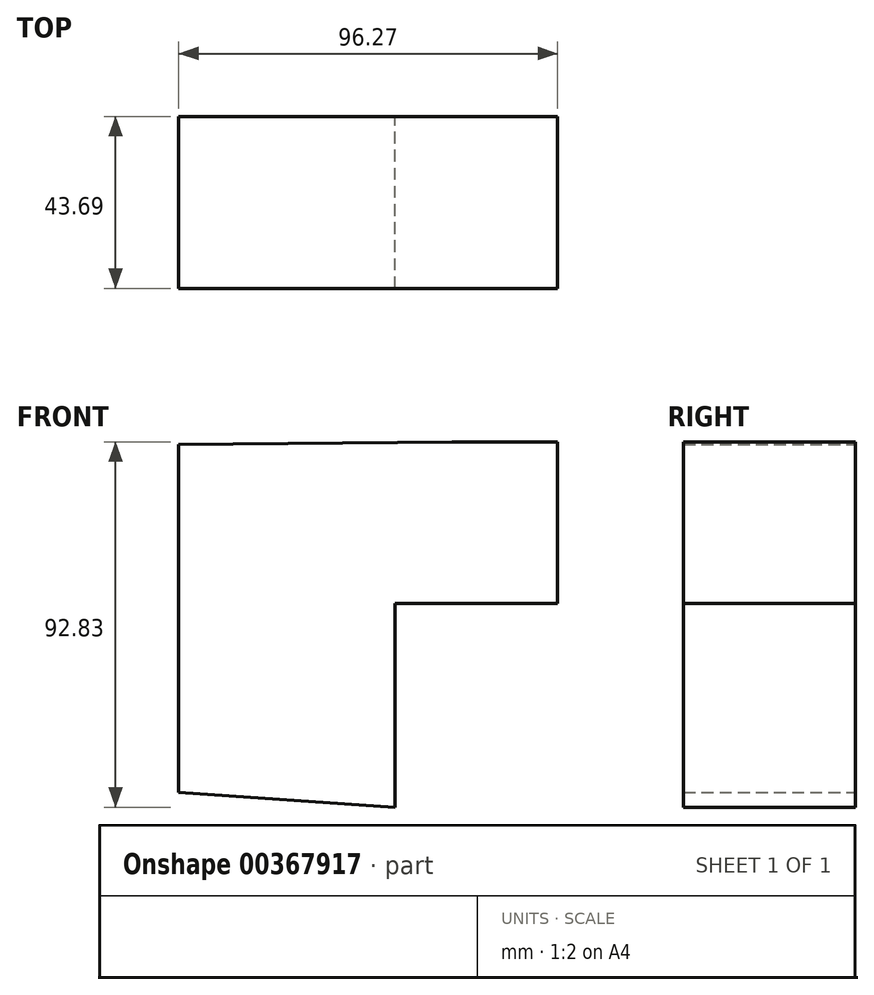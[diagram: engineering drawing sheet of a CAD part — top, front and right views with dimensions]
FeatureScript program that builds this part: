
annotation { "Feature Type Name" : "Feature", "Feature Type Description" : "" }
export const myFeature = defineFeature(function(context is Context, id is Id, definition is map)
    precondition{}
    {
        {
            var Q0;
            Q0=qCreatedBy(makeId("Front.planeOp"),FACE);
            var sketch = newSketch(context, id + "F0", { "sketchPlane" : qUnion([Q0])});
            skLineSegment(sketch, "E0", {"start": v(14.38, 41.1) * mm, "end": v(41.26, 41.1) * mm});
            skLineSegment(sketch, "E1", {"start": v(41.26, 41.1) * mm, "end": v(41.26, 0) * mm});
            skLineSegment(sketch, "E2", {"start": v(41.26, 0) * mm, "end": v(0, 0) * mm});
            skLineSegment(sketch, "E3", {"start": v(0, 0) * mm, "end": v(0, -51.73) * mm});
            skLineSegment(sketch, "E4", {"start": v(0, -51.73) * mm, "end": v(-55.01, -47.98) * mm});
            skLineSegment(sketch, "E5", {"start": v(-55.01, -47.98) * mm, "end": v(-55.01, 40.48) * mm});
            skLineSegment(sketch, "E6", {"start": v(-55.01, 40.48) * mm, "end": v(14.38, 41.1) * mm});
            skSolve(sketch);
        }
        {
            var Q0;
            Q0 = qSketchRegion(id + "F0", true);
            extrude(context, id + "F1", {"entities" : qUnion([Q0]), "depth" : 25.4 * mm});
        }
        {
            var Q0;
            Q0=makeQuery(id+"F1.opExtrude","CAP_FACE",FACE,{"disambiguationData":[OSD([sQuery(id+"F0.wireOp",EDGE,"E0"),sQuery(id+"F0.wireOp",EDGE,"E1"),sQuery(id+"F0.wireOp",EDGE,"E2"),sQuery(id+"F0.wireOp",EDGE,"E3"),sQuery(id+"F0.wireOp",EDGE,"E4"),sQuery(id+"F0.wireOp",EDGE,"E5"),sQuery(id+"F0.wireOp",EDGE,"E6")])],"isStart":false});
            extrude(context, id + "F2", {"entities" : qUnion([Q0]), "operationType" : NewBodyOperationType.ADD, "depth" : 18.29 * mm});
        }
    });
